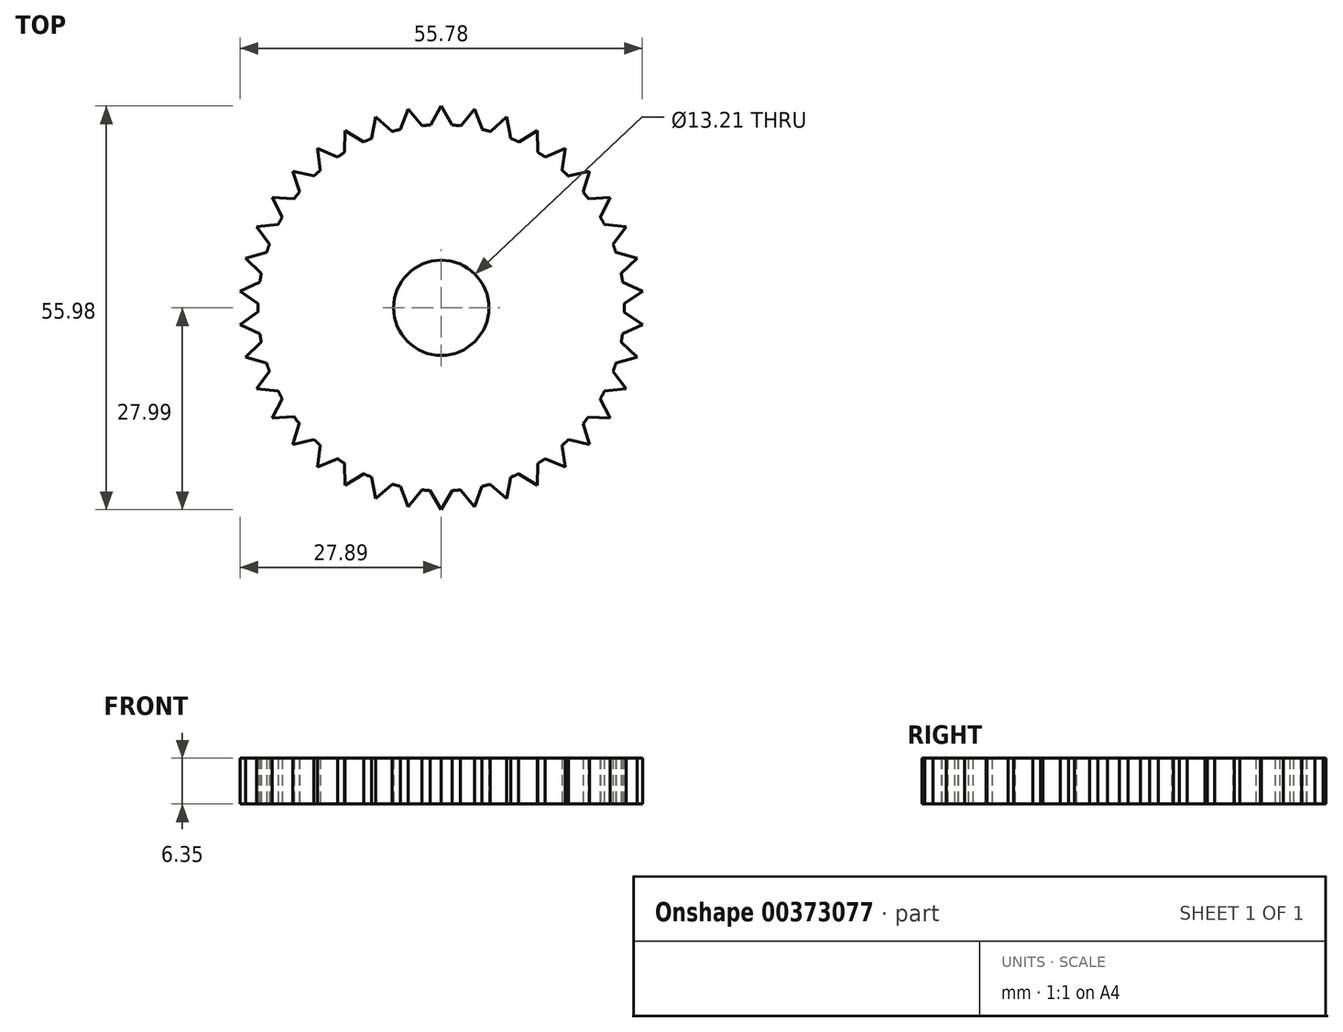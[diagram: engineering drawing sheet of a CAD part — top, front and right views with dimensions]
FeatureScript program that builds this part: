
annotation { "Feature Type Name" : "Feature", "Feature Type Description" : "" }
export const myFeature = defineFeature(function(context is Context, id is Id, definition is map)
    precondition{}
    {
        {
            var Q0;
            Q0=qCreatedBy(makeId("Top.planeOp"),FACE);
            var sketch = newSketch(context, id + "F0", { "sketchPlane" : qUnion([Q0])});
            skCircle(sketch, "E0", {"center": v(0, 0) * mm, "radius": 25.4 * mm});
            skCircle(sketch, "E1", {"center": v(0, 0) * mm, "radius": 6.6 * mm});
            skLineSegment(sketch, "E2", {"start": v(0, 25.4) * mm, "end": v(0, 27.99) * mm});
            skLineSegment(sketch, "E3", {"start": v(0, 27.99) * mm, "end": v(1.51, 25.35) * mm});
            skLineSegment(sketch, "E4", {"start": v(0, 27.99) * mm, "end": v(-1.5, 25.36) * mm});
            skLineSegment(sketch, "E5.1.0", {"start": v(-4.6, 27.6) * mm, "end": v(-5.65, 24.76) * mm});
            skLineSegment(sketch, "E5.1.1", {"start": v(-4.6, 27.6) * mm, "end": v(-2.68, 25.26) * mm});
            skLineSegment(sketch, "E5.2.0", {"start": v(-9.09, 26.47) * mm, "end": v(-9.65, 23.5) * mm});
            skLineSegment(sketch, "E5.2.1", {"start": v(-9.09, 26.47) * mm, "end": v(-6.8, 24.47) * mm});
            skLineSegment(sketch, "E5.3.0", {"start": v(-13.32, 24.62) * mm, "end": v(-13.39, 21.59) * mm});
            skLineSegment(sketch, "E5.3.1", {"start": v(-13.32, 24.62) * mm, "end": v(-10.74, 23.02) * mm});
            skLineSegment(sketch, "E5.4.0", {"start": v(-17.2, 22.09) * mm, "end": v(-16.76, 19.09) * mm});
            skLineSegment(sketch, "E5.4.1", {"start": v(-17.2, 22.09) * mm, "end": v(-14.38, 20.94) * mm});
            skLineSegment(sketch, "E5.5.0", {"start": v(-20.6, 18.96) * mm, "end": v(-19.67, 16.07) * mm});
            skLineSegment(sketch, "E5.5.1", {"start": v(-20.6, 18.96) * mm, "end": v(-17.63, 18.29) * mm});
            skLineSegment(sketch, "E5.6.0", {"start": v(-23.43, 15.3) * mm, "end": v(-22.05, 12.61) * mm});
            skLineSegment(sketch, "E5.6.1", {"start": v(-23.43, 15.3) * mm, "end": v(-20.4, 15.14) * mm});
            skLineSegment(sketch, "E5.7.0", {"start": v(-25.63, 11.24) * mm, "end": v(-23.82, 8.81) * mm});
            skLineSegment(sketch, "E5.7.1", {"start": v(-25.63, 11.24) * mm, "end": v(-22.61, 11.57) * mm});
            skLineSegment(sketch, "E5.8.0", {"start": v(-27.13, 6.87) * mm, "end": v(-24.95, 4.77) * mm});
            skLineSegment(sketch, "E5.8.1", {"start": v(-27.13, 6.87) * mm, "end": v(-24.2, 7.7) * mm});
            skLineSegment(sketch, "E5.9.0", {"start": v(-27.9, 2.31) * mm, "end": v(-25.4, 0.6) * mm});
            skLineSegment(sketch, "E5.9.1", {"start": v(-27.9, 2.31) * mm, "end": v(-25.14, 3.6) * mm});
            skLineSegment(sketch, "E5.10.0", {"start": v(-27.9, -2.31) * mm, "end": v(-25.15, -3.59) * mm});
            skLineSegment(sketch, "E5.10.1", {"start": v(-27.9, -2.31) * mm, "end": v(-25.4, -0.58) * mm});
            skLineSegment(sketch, "E5.11.0", {"start": v(-27.13, -6.87) * mm, "end": v(-24.21, -7.68) * mm});
            skLineSegment(sketch, "E5.11.1", {"start": v(-27.13, -6.87) * mm, "end": v(-24.95, -4.76) * mm});
            skLineSegment(sketch, "E5.12.0", {"start": v(-25.63, -11.24) * mm, "end": v(-22.62, -11.56) * mm});
            skLineSegment(sketch, "E5.12.1", {"start": v(-25.63, -11.24) * mm, "end": v(-23.83, -8.8) * mm});
            skLineSegment(sketch, "E5.13.0", {"start": v(-23.43, -15.3) * mm, "end": v(-20.4, -15.12) * mm});
            skLineSegment(sketch, "E5.13.1", {"start": v(-23.43, -15.3) * mm, "end": v(-22.05, -12.6) * mm});
            skLineSegment(sketch, "E5.14.0", {"start": v(-20.6, -18.96) * mm, "end": v(-17.64, -18.28) * mm});
            skLineSegment(sketch, "E5.14.1", {"start": v(-20.6, -18.96) * mm, "end": v(-19.68, -16.06) * mm});
            skLineSegment(sketch, "E5.15.0", {"start": v(-17.2, -22.09) * mm, "end": v(-14.4, -20.93) * mm});
            skLineSegment(sketch, "E5.15.1", {"start": v(-17.2, -22.09) * mm, "end": v(-16.77, -19.08) * mm});
            skLineSegment(sketch, "E5.16.0", {"start": v(-13.32, -24.62) * mm, "end": v(-10.75, -23.01) * mm});
            skLineSegment(sketch, "E5.16.1", {"start": v(-13.32, -24.62) * mm, "end": v(-13.4, -21.58) * mm});
            skLineSegment(sketch, "E5.17.0", {"start": v(-9.09, -26.47) * mm, "end": v(-6.82, -24.47) * mm});
            skLineSegment(sketch, "E5.17.1", {"start": v(-9.09, -26.47) * mm, "end": v(-9.66, -23.49) * mm});
            skLineSegment(sketch, "E5.18.0", {"start": v(-4.6, -27.6) * mm, "end": v(-2.7, -25.26) * mm});
            skLineSegment(sketch, "E5.18.1", {"start": v(-4.6, -27.6) * mm, "end": v(-5.67, -24.76) * mm});
            skLineSegment(sketch, "E5.19.0", {"start": v(0, -27.99) * mm, "end": v(1.5, -25.36) * mm});
            skLineSegment(sketch, "E5.19.1", {"start": v(0, -27.99) * mm, "end": v(-1.51, -25.35) * mm});
            skLineSegment(sketch, "E5.20.0", {"start": v(4.6, -27.6) * mm, "end": v(5.65, -24.76) * mm});
            skLineSegment(sketch, "E5.20.1", {"start": v(4.6, -27.6) * mm, "end": v(2.68, -25.26) * mm});
            skLineSegment(sketch, "E5.21.0", {"start": v(9.09, -26.47) * mm, "end": v(9.65, -23.5) * mm});
            skLineSegment(sketch, "E5.21.1", {"start": v(9.09, -26.47) * mm, "end": v(6.8, -24.47) * mm});
            skLineSegment(sketch, "E5.22.0", {"start": v(13.32, -24.62) * mm, "end": v(13.39, -21.59) * mm});
            skLineSegment(sketch, "E5.22.1", {"start": v(13.32, -24.62) * mm, "end": v(10.74, -23.02) * mm});
            skLineSegment(sketch, "E5.23.0", {"start": v(17.2, -22.09) * mm, "end": v(16.76, -19.09) * mm});
            skLineSegment(sketch, "E5.23.1", {"start": v(17.2, -22.09) * mm, "end": v(14.38, -20.94) * mm});
            skLineSegment(sketch, "E5.24.0", {"start": v(20.6, -18.96) * mm, "end": v(19.67, -16.07) * mm});
            skLineSegment(sketch, "E5.24.1", {"start": v(20.6, -18.96) * mm, "end": v(17.63, -18.29) * mm});
            skLineSegment(sketch, "E5.25.0", {"start": v(23.43, -15.3) * mm, "end": v(22.05, -12.61) * mm});
            skLineSegment(sketch, "E5.25.1", {"start": v(23.43, -15.3) * mm, "end": v(20.4, -15.14) * mm});
            skLineSegment(sketch, "E5.26.0", {"start": v(25.63, -11.24) * mm, "end": v(23.82, -8.81) * mm});
            skLineSegment(sketch, "E5.26.1", {"start": v(25.63, -11.24) * mm, "end": v(22.61, -11.57) * mm});
            skLineSegment(sketch, "E5.27.0", {"start": v(27.13, -6.87) * mm, "end": v(24.95, -4.77) * mm});
            skLineSegment(sketch, "E5.27.1", {"start": v(27.13, -6.87) * mm, "end": v(24.2, -7.7) * mm});
            skLineSegment(sketch, "E5.28.0", {"start": v(27.9, -2.31) * mm, "end": v(25.4, -0.6) * mm});
            skLineSegment(sketch, "E5.28.1", {"start": v(27.9, -2.31) * mm, "end": v(25.14, -3.6) * mm});
            skLineSegment(sketch, "E5.29.0", {"start": v(27.9, 2.31) * mm, "end": v(25.15, 3.59) * mm});
            skLineSegment(sketch, "E5.29.1", {"start": v(27.9, 2.31) * mm, "end": v(25.4, 0.58) * mm});
            skLineSegment(sketch, "E5.30.0", {"start": v(27.13, 6.87) * mm, "end": v(24.21, 7.68) * mm});
            skLineSegment(sketch, "E5.30.1", {"start": v(27.13, 6.87) * mm, "end": v(24.95, 4.76) * mm});
            skLineSegment(sketch, "E5.31.0", {"start": v(25.63, 11.24) * mm, "end": v(22.62, 11.56) * mm});
            skLineSegment(sketch, "E5.31.1", {"start": v(25.63, 11.24) * mm, "end": v(23.83, 8.8) * mm});
            skLineSegment(sketch, "E5.32.0", {"start": v(23.43, 15.3) * mm, "end": v(20.4, 15.12) * mm});
            skLineSegment(sketch, "E5.32.1", {"start": v(23.43, 15.3) * mm, "end": v(22.05, 12.6) * mm});
            skLineSegment(sketch, "E5.33.0", {"start": v(20.6, 18.96) * mm, "end": v(17.64, 18.28) * mm});
            skLineSegment(sketch, "E5.33.1", {"start": v(20.6, 18.96) * mm, "end": v(19.68, 16.06) * mm});
            skLineSegment(sketch, "E5.34.0", {"start": v(17.2, 22.09) * mm, "end": v(14.4, 20.93) * mm});
            skLineSegment(sketch, "E5.34.1", {"start": v(17.2, 22.09) * mm, "end": v(16.77, 19.08) * mm});
            skLineSegment(sketch, "E5.35.0", {"start": v(13.32, 24.62) * mm, "end": v(10.75, 23.01) * mm});
            skLineSegment(sketch, "E5.35.1", {"start": v(13.32, 24.62) * mm, "end": v(13.4, 21.58) * mm});
            skLineSegment(sketch, "E5.36.0", {"start": v(9.09, 26.47) * mm, "end": v(6.82, 24.47) * mm});
            skLineSegment(sketch, "E5.36.1", {"start": v(9.09, 26.47) * mm, "end": v(9.66, 23.49) * mm});
            skLineSegment(sketch, "E5.37.0", {"start": v(4.6, 27.6) * mm, "end": v(2.7, 25.26) * mm});
            skLineSegment(sketch, "E5.37.1", {"start": v(4.6, 27.6) * mm, "end": v(5.67, 24.76) * mm});
            skSolve(sketch);
        }
        {
            var Q0;
            Q0 = qSketchRegion(id + "F0", true);
            extrude(context, id + "F1", {"entities" : qUnion([Q0]), "depth" : 6.35 * mm});
        }
    });
